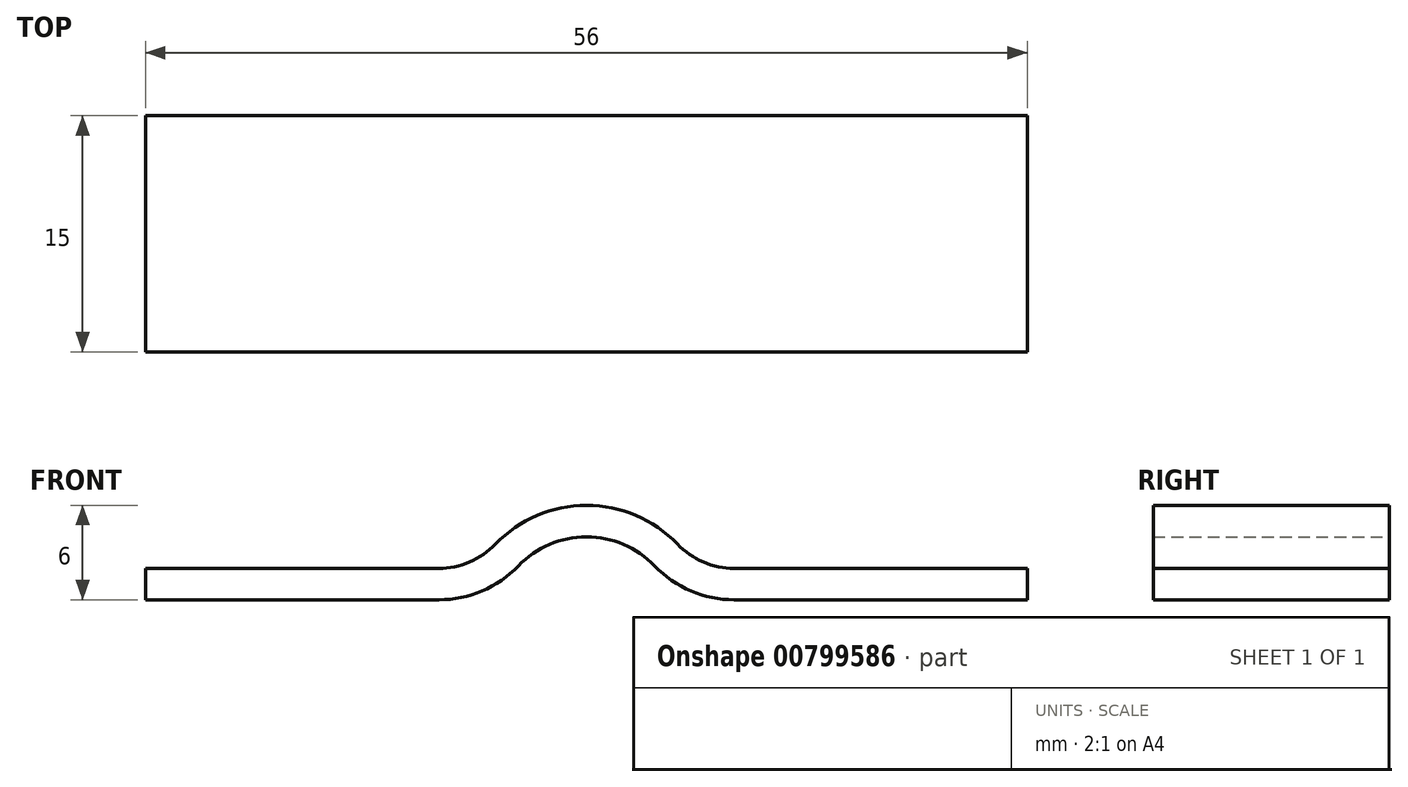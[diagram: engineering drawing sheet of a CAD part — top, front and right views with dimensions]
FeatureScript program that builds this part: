
annotation { "Feature Type Name" : "Feature", "Feature Type Description" : "" }
export const myFeature = defineFeature(function(context is Context, id is Id, definition is map)
    precondition{}
    {
        {
            var Q0;
            Q0=qCreatedBy(makeId("Front.planeOp"),FACE);
            var sketch = newSketch(context, id + "F0", { "sketchPlane" : qUnion([Q0])});
            skLineSegment(sketch, "E0", {"start": v(-28, 0) * mm, "end": v(-9.38, 0) * mm});
            skLineSegment(sketch, "E1", {"start": v(-9.38, 4) * mm, "end": v(-28, 4) * mm});
            skLineSegment(sketch, "E2", {"start": v(-28, 4) * mm, "end": v(-28, 0) * mm});
            skLineSegment(sketch, "E3", {"start": v(9.38, 0) * mm, "end": v(28, 0) * mm});
            skLineSegment(sketch, "E4", {"start": v(28, 0) * mm, "end": v(28, 4) * mm});
            skLineSegment(sketch, "E5", {"start": v(28, 4) * mm, "end": v(9.38, 4) * mm});
            skArc(sketch, "E6", {"start": v(7.22, 4.92) * mm, "mid": v(0, 8) * mm, "end": v(-7.22, 4.92) * mm});
            skArc(sketch, "E7", {"start": v(4.33, 2.15) * mm, "mid": v(0, 4) * mm, "end": v(-4.33, 2.15) * mm});
            skLineSegment(sketch, "E8", {"start": v(-8.19, 8) * mm, "end": v(18.85, 8) * mm, "construction": true});
            skPoint(sketch, "E9.visualSharp", {"position": v(-8, 4) * mm});
            skArc(sketch, "E9.filletArc", {"start": v(-9.38, 4) * mm, "mid": v(-8.2, 4.24) * mm, "end": v(-7.22, 4.92) * mm});
            skPoint(sketch, "E10.visualSharp", {"position": v(8, 4) * mm});
            skArc(sketch, "E10.filletArc", {"start": v(7.22, 4.92) * mm, "mid": v(8.2, 4.24) * mm, "end": v(9.38, 4) * mm});
            skPoint(sketch, "E11.visualSharp", {"position": v(5.66, 0) * mm});
            skArc(sketch, "E11.filletArc", {"start": v(4.33, 2.15) * mm, "mid": v(6.64, 0.56) * mm, "end": v(9.38, 0) * mm});
            skPoint(sketch, "E12.visualSharp", {"position": v(-5.66, 0) * mm});
            skArc(sketch, "E12.filletArc", {"start": v(-9.38, 0) * mm, "mid": v(-6.64, 0.56) * mm, "end": v(-4.33, 2.15) * mm});
            skSolve(sketch);
        }
        {
            var Q0;
            Q0=makeQuery(id+"F0.imprint","IMPRINT",FACE,{"disambiguationData":[TD([[makeQuery(id+"F0.imprint","IMPRINT",EDGE,{"derivedFrom":sQuery(id+"F0.wireOp",EDGE,"E0")}),1.0]])]});
            var sketch = newSketch(context, id + "F1", { "sketchPlane" : qUnion([Q0])});
            skSolve(sketch);
        }
        {
            var Q0;
            Q0 = qSketchRegion(id + "F1", true);
            var Q1;
            Q1=makeQuery(id+"F0.imprint","IMPRINT",FACE,{"disambiguationData":[TD([[makeQuery(id+"F0.imprint","IMPRINT",EDGE,{"derivedFrom":sQuery(id+"F0.wireOp",EDGE,"E0")}),1.0]])]});
            extrude(context, id + "F2", {"entities" : qUnion([Q0, Q1]), "depth" : 15 * mm, "offsetDistance" : 25 * mm});
        }
        {
            var Q0;
            Q0=makeQuery(id+"F2.opExtrude","CAP_FACE",FACE,{"disambiguationData":[OSD([sQuery(id+"F0.wireOp",EDGE,"E0"),sQuery(id+"F0.wireOp",EDGE,"E1"),sQuery(id+"F0.wireOp",EDGE,"E2"),sQuery(id+"F0.wireOp",EDGE,"E3"),sQuery(id+"F0.wireOp",EDGE,"E4"),sQuery(id+"F0.wireOp",EDGE,"E5"),sQuery(id+"F0.wireOp",EDGE,"E6"),sQuery(id+"F0.wireOp",EDGE,"E7"),sQuery(id+"F0.wireOp",EDGE,"E9.filletArc"),sQuery(id+"F0.wireOp",EDGE,"E10.filletArc"),sQuery(id+"F0.wireOp",EDGE,"E11.filletArc"),sQuery(id+"F0.wireOp",EDGE,"E12.filletArc")])],"isStart":false});
            var sketch = newSketch(context, id + "F3", { "sketchPlane" : qUnion([Q0])});
            skLineSegment(sketch, "E13.0", {"start": v(-9.38, 4) * mm, "end": v(-28, 4) * mm});
            skArc(sketch, "E13.1", {"start": v(-9.38, 4) * mm, "mid": v(-8.2, 4.24) * mm, "end": v(-7.22, 4.92) * mm});
            skArc(sketch, "E13.2", {"start": v(7.22, 4.92) * mm, "mid": v(0, 8) * mm, "end": v(-7.22, 4.92) * mm});
            skArc(sketch, "E13.3", {"start": v(7.22, 4.92) * mm, "mid": v(8.2, 4.24) * mm, "end": v(9.38, 4) * mm});
            skLineSegment(sketch, "E13.4", {"start": v(28, 4) * mm, "end": v(9.38, 4) * mm});
            skLineSegment(sketch, "E14.0", {"start": v(-9.38, 2) * mm, "end": v(-28, 2) * mm});
            skLineSegment(sketch, "E14.1", {"start": v(28, 2) * mm, "end": v(9.38, 2) * mm});
            skArc(sketch, "E14.2", {"start": v(5.77, 3.54) * mm, "mid": v(7.42, 2.4) * mm, "end": v(9.38, 2) * mm});
            skArc(sketch, "E14.3", {"start": v(5.77, 3.54) * mm, "mid": v(0, 6) * mm, "end": v(-5.77, 3.54) * mm});
            skArc(sketch, "E14.4", {"start": v(-9.38, 2) * mm, "mid": v(-7.42, 2.4) * mm, "end": v(-5.77, 3.54) * mm});
            skLineSegment(sketch, "E15", {"start": v(-28, 4) * mm, "end": v(-28, 2) * mm});
            skLineSegment(sketch, "E16", {"start": v(28, 4) * mm, "end": v(28, 2) * mm});
            skSolve(sketch);
        }
        {
            var Q0;
            Q0=makeQuery(id+"F3.imprint","IMPRINT",FACE,{"disambiguationData":[TD([[makeQuery(id+"F3.imprint","IMPRINT",EDGE,{"derivedFrom":sQuery(id+"F3.wireOp",EDGE,"E13.0")}),1.0]])]});
            extrude(context, id + "F4", {"entities" : qUnion([Q0]), "operationType" : NewBodyOperationType.REMOVE, "oppositeDirection" : true, "depth" : 25 * mm, "offsetDistance" : 25 * mm});
        }
    });
